annotation { "Feature Type Name" : "Feature", "Feature Type Description" : "" }
export const myFeature = defineFeature(function(context is Context, id is Id, definition is map)
    precondition{}
    {
        {
            var Q0;
            Q0=qCreatedBy(makeId("Top.planeOp"),FACE);
            var sketch = newSketch(context, id + "F0", { "sketchPlane" : qUnion([Q0])});
            skLineSegment(sketch, "E0.left", {"start": v(0, 0) * mm, "end": v(0, 12.7) * mm});
            skLineSegment(sketch, "E0.right", {"start": v(2.54, 0) * mm, "end": v(2.54, 12.7) * mm});
            skLineSegment(sketch, "E1", {"start": v(0.5, -3.89) * mm, "end": v(0.45, -3.81) * mm});
            skLineSegment(sketch, "E2", {"start": v(0.45, -3.81) * mm, "end": v(0.5, -3.89) * mm});
            skCircle(sketch, "E3", {"center": v(1.27, -2.54) * mm, "radius": 3.33 * mm});
            skLineSegment(sketch, "E4.0", {"start": v(0.12, 0.18) * mm, "end": v(3.05, -0.18) * mm});
            skLineSegment(sketch, "E4.1", {"start": v(3.05, -0.18) * mm, "end": v(4.2, -2.9) * mm});
            skLineSegment(sketch, "E4.2", {"start": v(4.2, -2.9) * mm, "end": v(2.42, -5.26) * mm});
            skLineSegment(sketch, "E4.3", {"start": v(2.42, -5.26) * mm, "end": v(-0.5, -4.9) * mm});
            skLineSegment(sketch, "E4.4", {"start": v(-0.5, -4.9) * mm, "end": v(-1.66, -2.18) * mm});
            skLineSegment(sketch, "E4.5", {"start": v(-1.66, -2.18) * mm, "end": v(0.12, 0.18) * mm});
            skPoint(sketch, "E4.0.midPoint", {"position": v(1.58, 0) * mm});
            skLineSegment(sketch, "E5.0", {"start": v(-1.65, 15.13) * mm, "end": v(-0.21, 17.61) * mm});
            skLineSegment(sketch, "E5.1", {"start": v(-0.21, 17.61) * mm, "end": v(2.65, 17.61) * mm});
            skLineSegment(sketch, "E5.3", {"start": v(4.08, 15.13) * mm, "end": v(2.65, 12.65) * mm});
            skLineSegment(sketch, "E5.5", {"start": v(-0.21, 12.65) * mm, "end": v(-1.65, 15.13) * mm});
            skPoint(sketch, "E5.0.midPoint", {"position": v(-0.93, 16.37) * mm});
            skLineSegment(sketch, "E6", {"start": v(-0.21, 12.65) * mm, "end": v(2.65, 12.65) * mm});
            skLineSegment(sketch, "E7", {"start": v(2.65, 17.61) * mm, "end": v(3.16, 17.61) * mm});
            skLineSegment(sketch, "E8", {"start": v(4.08, 15.13) * mm, "end": v(4.33, 15.57) * mm});
            skArc(sketch, "E9", {"start": v(3.16, 17.61) * mm, "mid": v(-1.51, 13.56) * mm, "end": v(4.33, 15.57) * mm});
            skSolve(sketch);
        }
        {
            var Q0;
            Q0 = qSketchRegion(id + "F0", true);
            extrude(context, id + "F1", {"entities" : qUnion([Q0]), "depth" : 1.27 * mm, "offsetDistance" : 25.4 * mm});
        }
        {
            var Q0;
            Q0=qCreatedBy(makeId("Right.planeOp"),FACE);
            var sketch = newSketch(context, id + "F2", { "sketchPlane" : qUnion([Q0])});
            skSolve(sketch);
        }
        {
            var Q0;
            Q0 = qSketchRegion(id + "F0", true);
            extrude(context, id + "F3", {"entities" : qUnion([Q0]), "operationType" : NewBodyOperationType.ADD, "depth" : 1.52 * mm, "offsetDistance" : 25.4 * mm});
        }
        {
            var Q0;
            Q0 = qSketchRegion(id + "F0", true);
            extrude(context, id + "F4", {"entities" : qUnion([Q0]), "operationType" : NewBodyOperationType.ADD, "depth" : 1.78 * mm, "offsetDistance" : 25.4 * mm});
        }
        {
            var Q0;
            Q0 = qSketchRegion(id + "F0", true);
            var Q1;
            Q1 = qSketchRegion(id + "F2", true);
            extrude(context, id + "F5", {"entities" : qUnion([Q0, Q1]), "operationType" : NewBodyOperationType.ADD, "depth" : 2.03 * mm, "offsetDistance" : 25.4 * mm});
        }
        {
            var Q0;
            Q0=makeQuery(id+"F5.opExtrude","CAP_FACE",FACE,{"disambiguationData":[OSD([sQuery(id+"F0.wireOp",EDGE,"E0.left"),sQuery(id+"F0.wireOp",EDGE,"E0.right"),sQuery(id+"F0.wireOp",EDGE,"E3"),sQuery(id+"F0.wireOp",EDGE,"E4.1"),sQuery(id+"F0.wireOp",EDGE,"E4.3"),sQuery(id+"F0.wireOp",EDGE,"E4.5"),sQuery(id+"F0.wireOp",EDGE,"E4.4"),sQuery(id+"F0.wireOp",EDGE,"E4.0"),sQuery(id+"F0.wireOp",EDGE,"E4.2"),sQuery(id+"F0.wireOp",EDGE,"E5.0"),sQuery(id+"F0.wireOp",EDGE,"E5.1"),sQuery(id+"F0.wireOp",EDGE,"E5.3"),sQuery(id+"F0.wireOp",EDGE,"E5.5"),sQuery(id+"F0.wireOp",EDGE,"E6"),sQuery(id+"F0.wireOp",EDGE,"E7"),sQuery(id+"F0.wireOp",EDGE,"E8"),sQuery(id+"F0.wireOp",EDGE,"E9")])],"isStart":false});
            var sketch = newSketch(context, id + "F6", { "sketchPlane" : qUnion([Q0])});
            skText(sketch, "E10", { "text": "Stay Fresh\nPaRtH tAiLoR", "fontName": "OpenSans-Regular.ttf"});
            const initialGuessF6  = {"E10": [0.0009, 0.00054, 0, 1, 0.0009]};
            skSetInitialGuess(sketch, initialGuessF6);
            skSolve(sketch);
        }
        {
            var Q0;
            Q0 = qSketchRegion(id + "F6", true);
            extrude(context, id + "F7", {"entities" : qUnion([Q0]), "operationType" : NewBodyOperationType.ADD, "depth" : 0.25 * mm, "offsetDistance" : 25.4 * mm});
        }
    });